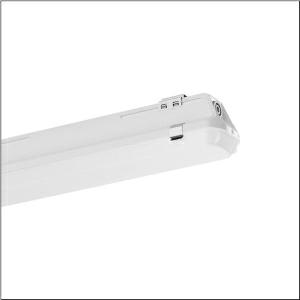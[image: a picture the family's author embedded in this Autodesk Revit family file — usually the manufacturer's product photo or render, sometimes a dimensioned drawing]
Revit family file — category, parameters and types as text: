
# Revit family: monsun_r__11_51fp20ep460h_939a
name_source: partatom
category: Lighting Fixtures
units: mm (PartAtom-declared; Revit-internal decimal feet)

## family parameters
Cut with Voids When Loaded = No
Host = Face
Light Source = No
Part Type = Normal
Room Calculation Point = No
Round Connector Dimension = Use Diameter
Shared = No

## types (1)
- --- (1 x LED, 5450 lm, 34.6 W, 4000K)
    Apparent Load = 35 VA
    CIE Flux Codes = 45 75 93 94 100
    Color Rendering = 80
    Color Temperature = 4000K
    Default Elevation = 1800 mm
    Description = Monsun® 11, damp-proof luminaire, chain hanger, primary optical cover: enclosure, of PC, light emission: direct distribution, primary light characteristic: symmetric, installation type: suspended mounting, surface-mounted, horizontal mounting, vertical mounting, LED, rated luminous flux: 5.450lm, luminous efficacy: 158lm/W, light colour: 840, colour temperature: 4000K, control gear: ECG DALI, with terminal, 5-pole, max. 2.5mm², mains connection: 220..240V, AC, 50/60Hz, rated input power: 35W, luminaire housing, of glass-fibre reinforced polyester, uncoated, bright grey, incl. chain hanger, length: 1.590mm, width: 90mm, height: 88mm, clip for enclosure, of stainless steel (V2A), ceiling mounting element, of stainless steel (V2A), chain hanger, of stainless steel (V2A), protection rating (complete): IP66, insulation class (complete): insulation class I (protective earthing), certification: CE, ENEC, VDE, UKCA, protection symbol: D, impact resistance: IK08, permissible operating ambient temperature: -25..+40°C, standard: EN 50419, EN 60598-2-1, no direct snow, no direct sun, no direct rain, for indoor or canopied outdoor use, corresponds to IFS (International Featured Standards) requirements for safety and quality in the food industry, contact your sales advisor before using the luminaires in applications with unclear chemical exposure, large temperature fluctuations or condensation-forming humidity, LABS conformity tested according to VDMA 24364:2018-05, packaging unit: 1 piece
    Height = 89 mm
    Lamp = 1 x LED
    Lamp Light Flux = 5450 lm
    Lamp Power = 34.6 W
    Lamp count = 1
    Length = 1590 mm
    Luminous efficacy = 158 lm/W
    Manufacturer = Siteco
    ModVariant = No
    Model = 51FP20EP460H
    Mounting Place = Ceiling
    Mounting Type = Surface mounted
    Number of Poles = 1
    OnlyDefault = Yes
    Power Factor = 1
    Product Name = Monsun® 11
    Product group = damp-proof luminaire
    ProductGroupID = 300
    Protection Class = Protection class I
    Protection Degree = IP 66
    RLX_Detail_Level = 1
    RLX_Emergency_Light_Flux = 0 lm
    RLX_Emergency_Type = 0
    RLX_Emergency_Type_DB = No
    RlxData = <blob elided: 92257 chars, md5=a8c7629d>
    Socket = socket
    Standby Power = 0 W
    System Light Flux = 5450 lm
    System Power = 35 W
    Type Comments = factory setting: luminous flux: 100 % | dim-lin: 254 | 232 mA
    Type Image = l_1004748.jpg
    URL = http://relux.com
    VarID = @adj_140525
    Voltage = 0 V
    Weight = 0.00 kg
    Width = 90 mm

## geometry (parser evidence)
native form markers: Blend x4, Sweep x12
no freeform markers — native parametric forms only
